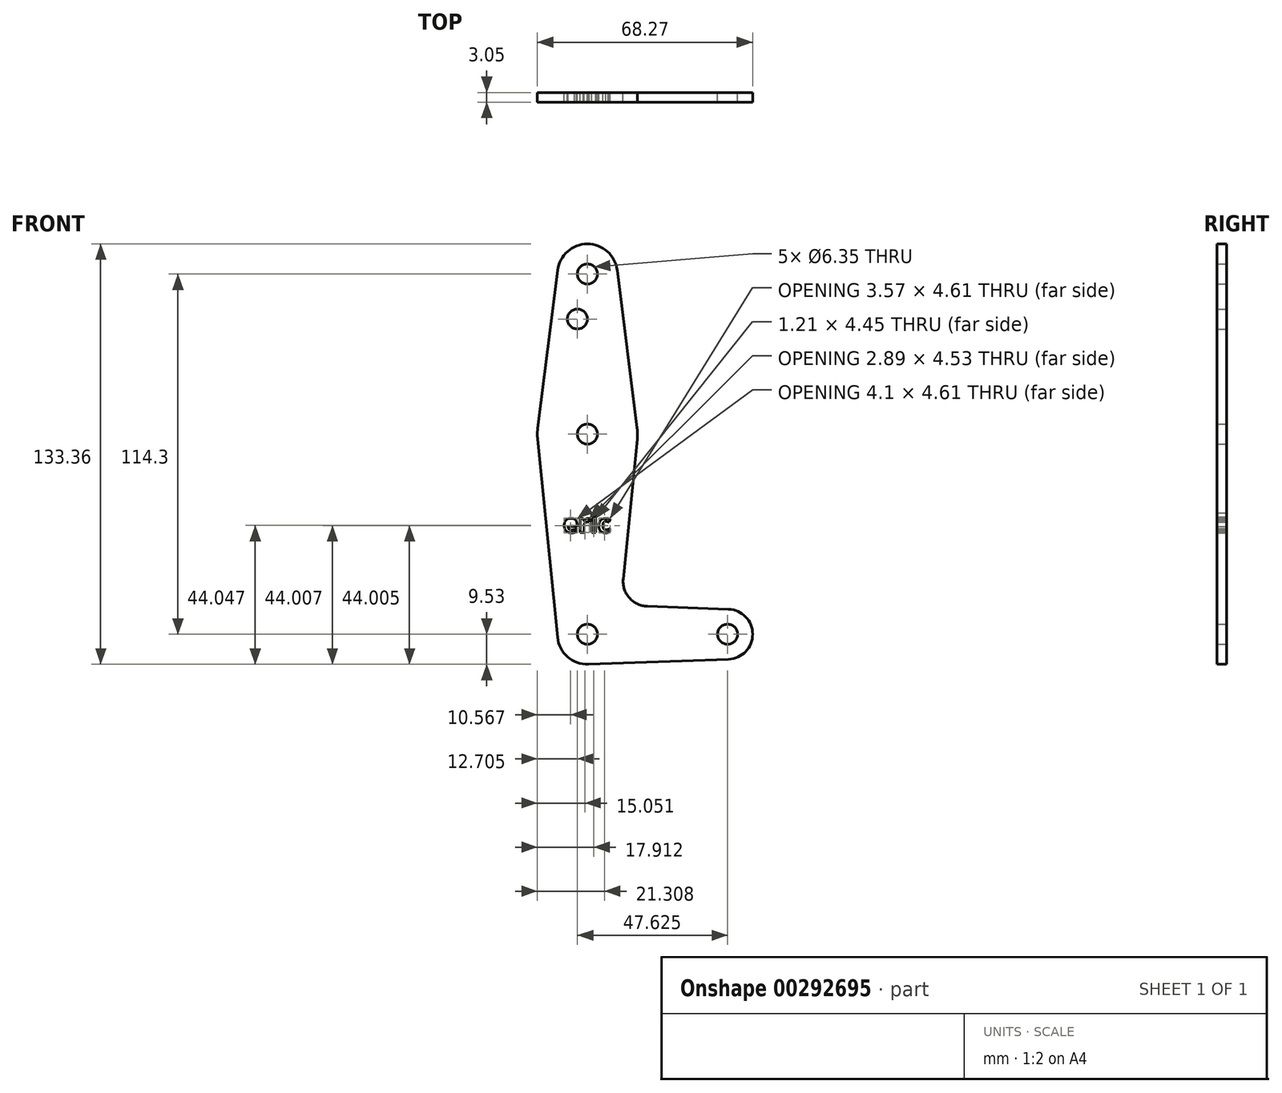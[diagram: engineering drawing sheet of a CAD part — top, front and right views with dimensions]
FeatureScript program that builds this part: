
annotation { "Feature Type Name" : "Feature", "Feature Type Description" : "" }
export const myFeature = defineFeature(function(context is Context, id is Id, definition is map)
    precondition{}
    {
        {
            var Q0;
            Q0=qCreatedBy(makeId("Front.planeOp"),FACE);
            var sketch = newSketch(context, id + "F0", { "sketchPlane" : qUnion([Q0])});
            skLineSegment(sketch, "E0", {"start": v(0, 0) * mm, "end": v(44.45, 0) * mm, "construction": true});
            skLineSegment(sketch, "E1", {"start": v(0, 0) * mm, "end": v(0, 114.3) * mm, "construction": true});
            skCircle(sketch, "E2", {"center": v(44.45, 0) * mm, "radius": 7.94 * mm});
            skCircle(sketch, "E3", {"center": v(0, 0) * mm, "radius": 9.53 * mm});
            skCircle(sketch, "E4", {"center": v(0, 63.5) * mm, "radius": 15.88 * mm});
            skCircle(sketch, "E5", {"center": v(0, 114.3) * mm, "radius": 9.53 * mm});
            skLineSegment(sketch, "E6", {"start": v(-9.45, 115.5) * mm, "end": v(-15.75, 65.48) * mm});
            skLineSegment(sketch, "E7", {"start": v(9.45, 115.5) * mm, "end": v(15.75, 65.48) * mm});
            skLineSegment(sketch, "E8", {"start": v(18.97, 8.85) * mm, "end": v(44.73, 7.93) * mm});
            skLineSegment(sketch, "E9", {"start": v(0.34, -9.52) * mm, "end": v(44.73, -7.93) * mm});
            skCircle(sketch, "E10", {"center": v(0, 114.3) * mm, "radius": 3.18 * mm});
            skCircle(sketch, "E11", {"center": v(0, 63.5) * mm, "radius": 3.18 * mm});
            skCircle(sketch, "E12", {"center": v(0, 0) * mm, "radius": 3.18 * mm});
            skCircle(sketch, "E13", {"center": v(44.45, 0) * mm, "radius": 3.18 * mm});
            skCircle(sketch, "E14", {"center": v(-3.18, 100.03) * mm, "radius": 3.18 * mm});
            skLineSegment(sketch, "E15.trimOffspring", {"start": v(11.34, 17.6) * mm, "end": v(15.8, 61.91) * mm});
            skArc(sketch, "E16.filletArc", {"start": v(11.34, 17.6) * mm, "mid": v(13.26, 11.57) * mm, "end": v(18.97, 8.85) * mm});
            skLineSegment(sketch, "E17", {"start": v(-15.8, 61.91) * mm, "end": v(-9.48, -0.95) * mm});
            skText(sketch, "E18", { "text": "eric", "fontName": "OpenSans-Bold.ttf"});
            const initialGuessF0  = {"E18": [-0.00773, 0.03225, 1, 0, 0.00587]};
            skSetInitialGuess(sketch, initialGuessF0);
            skSolve(sketch);
        }
        {
            var Q0;
            Q0 = qSketchRegion(id + "F0", true);
            extrude(context, id + "F1", {"entities" : qUnion([Q0]), "depth" : 3.05 * mm});
        }
    });
